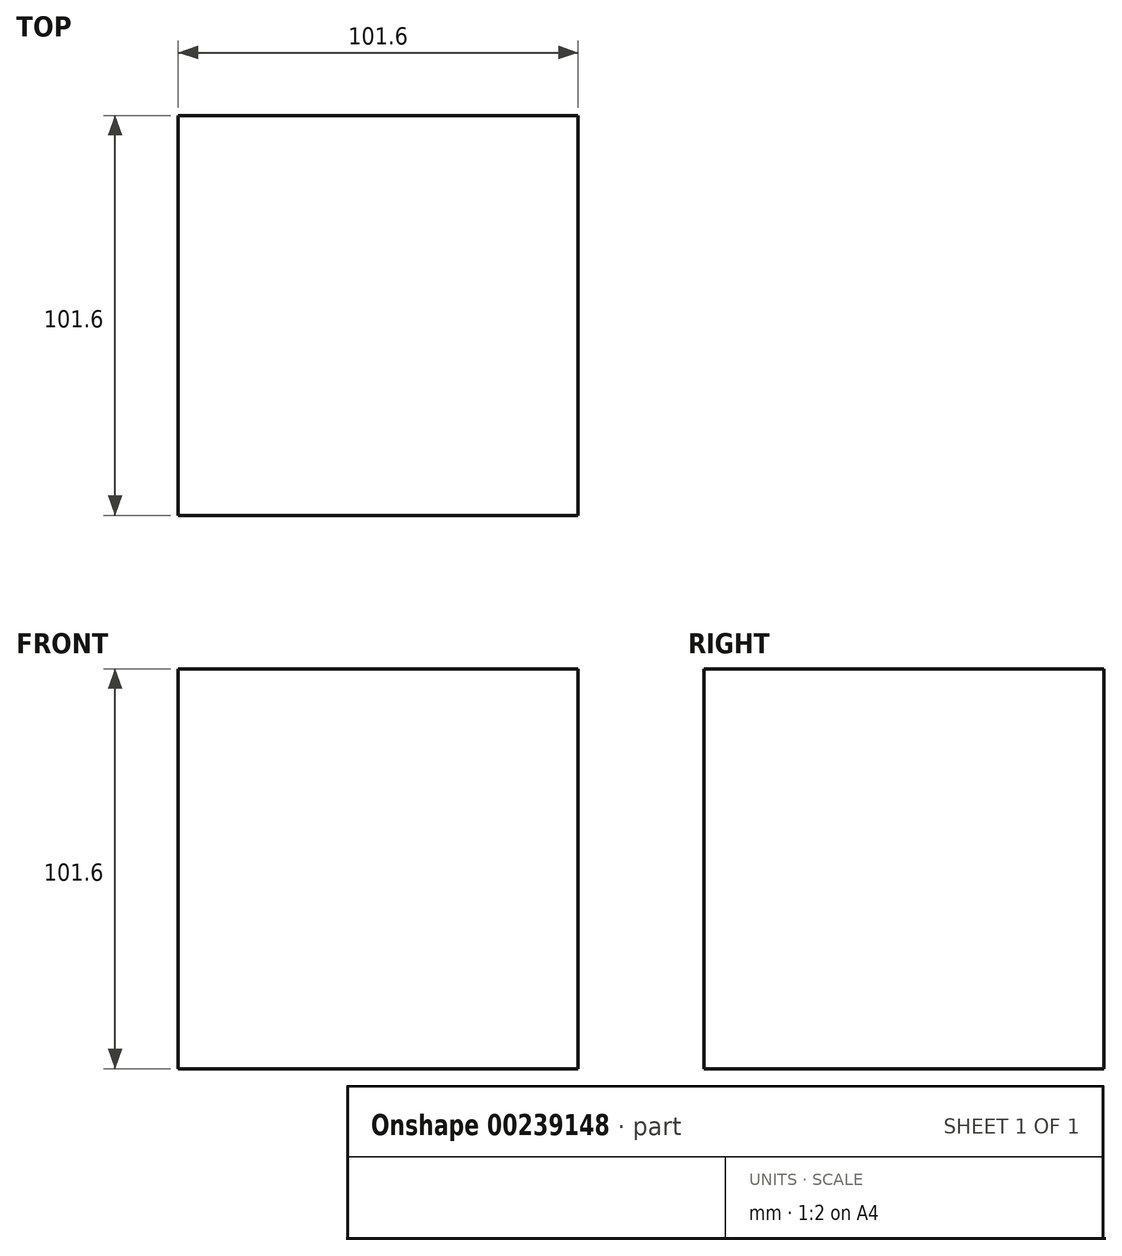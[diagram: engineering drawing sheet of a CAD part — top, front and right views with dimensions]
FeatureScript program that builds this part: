
annotation { "Feature Type Name" : "Feature", "Feature Type Description" : "" }
export const myFeature = defineFeature(function(context is Context, id is Id, definition is map)
    precondition{}
    {
        {
            var Q0;
            Q0=qCreatedBy(makeId("Front.planeOp"),FACE);
            var sketch = newSketch(context, id + "F0", { "sketchPlane" : qUnion([Q0])});
            skLineSegment(sketch, "E0.bottom", {"start": v(-50.8, 50.8) * mm, "end": v(50.8, 50.8) * mm});
            skLineSegment(sketch, "E0.top", {"start": v(-50.8, -50.8) * mm, "end": v(50.8, -50.8) * mm});
            skLineSegment(sketch, "E0.left", {"start": v(-50.8, 50.8) * mm, "end": v(-50.8, -50.8) * mm});
            skLineSegment(sketch, "E0.right", {"start": v(50.8, 50.8) * mm, "end": v(50.8, -50.8) * mm});
            skPoint(sketch, "E0.middle", {"position": v(0, 0) * mm});
            skSolve(sketch);
        }
        {
            var Q0;
            Q0 = qSketchRegion(id + "F0", true);
            extrude(context, id + "F1", {"entities" : qUnion([Q0]), "endBound" : BoundingType.SYMMETRIC, "depth" : 101.6 * mm});
        }
    });
